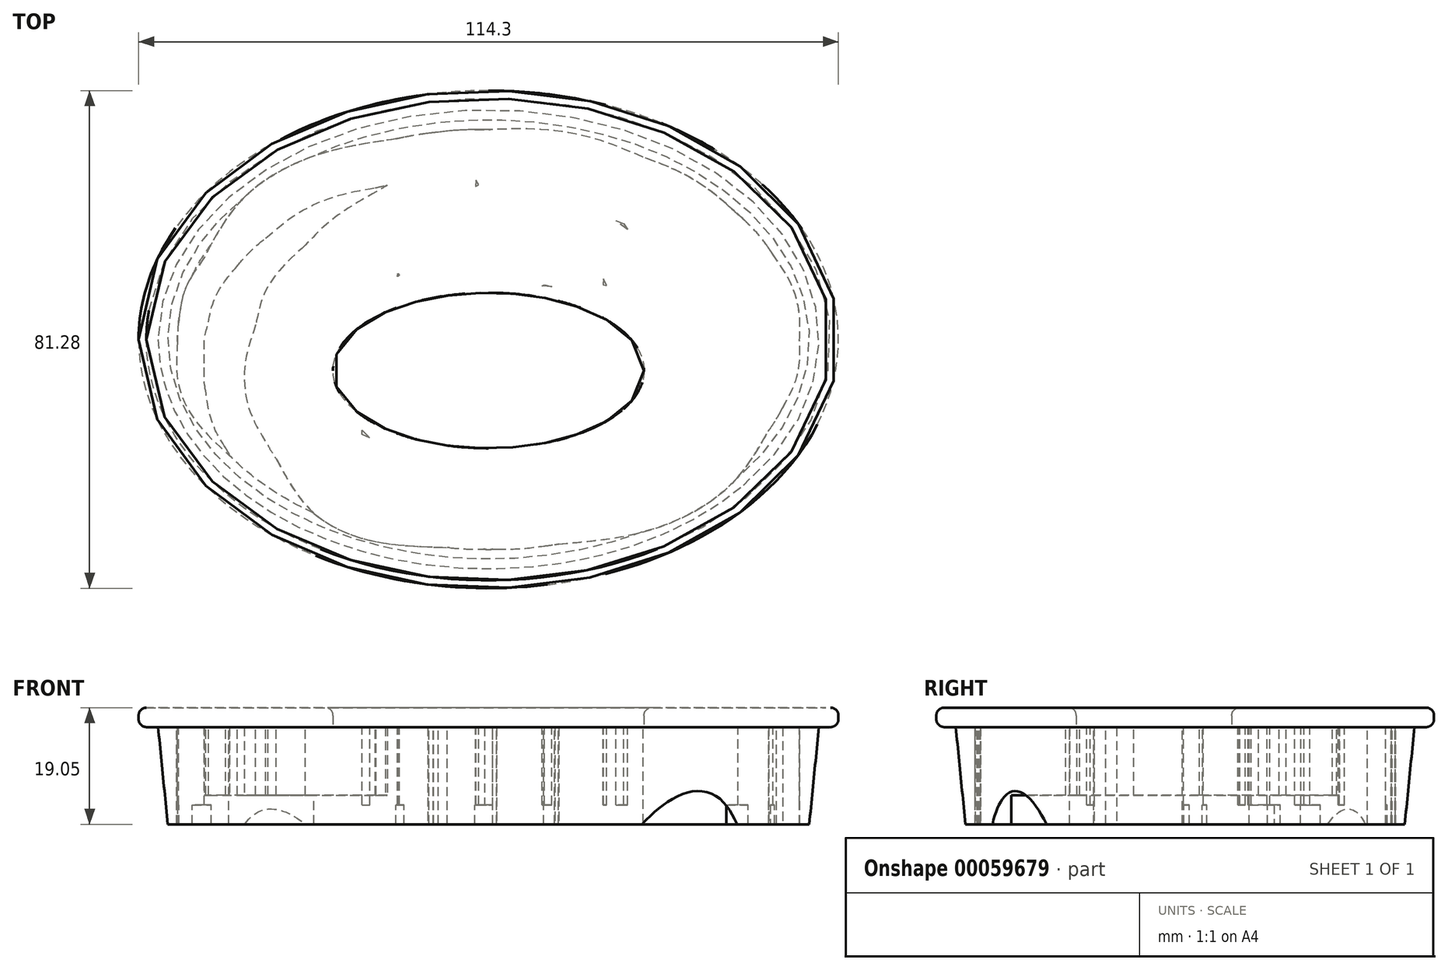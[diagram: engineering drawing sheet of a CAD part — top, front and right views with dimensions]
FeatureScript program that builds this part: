
annotation { "Feature Type Name" : "Feature", "Feature Type Description" : "" }
export const myFeature = defineFeature(function(context is Context, id is Id, definition is map)
    precondition{}
    {
        {
            var Q0;
            Q0=qCreatedBy(makeId("Top.planeOp"),FACE);
            var sketch = newSketch(context, id + "F0", { "sketchPlane" : qUnion([Q0])});
            skEllipse(sketch, "E0", {"center": v(0, 0) * mm, "majorRadius": 37.47 * mm, "minorRadius": 53.97 * mm, "majorAxis": v(0, 1)});
            skSolve(sketch);
        }
        {
            var Q0;
            Q0=makeQuery(id+"F0.imprint","IMPRINT",FACE,{"disambiguationData":[TD([[makeQuery(id+"F0.imprint","IMPRINT",EDGE,{"derivedFrom":sQuery(id+"F0.wireOp",EDGE,"E0")}),1.0]])]});
            extrude(context, id + "F1", {"entities" : qUnion([Q0]), "depth" : 12.7 * mm});
        }
        {
            var Q0;
            Q0=makeQuery(id+"F1.opExtrude","CAP_FACE",FACE,{"disambiguationData":[OSD([sQuery(id+"F0.wireOp",EDGE,"E0")])],"isStart":false});
            var sketch = newSketch(context, id + "F2", { "sketchPlane" : qUnion([Q0])});
            skFitSpline(sketch, "E1", {"points": [v(0.65, 34.29) * mm, v(0.15, 34.29) * mm, v(-0.36, 34.29) * mm, v(-0.87, 34.28) * mm]});
            skFitSpline(sketch, "E2", {"points": [v(-0.87, 34.28) * mm, v(-3.56, 34.22) * mm, v(-5.92, 34.09) * mm, v(-8.17, 33.85) * mm]});
            skFitSpline(sketch, "E3", {"points": [v(-8.17, 33.85) * mm, v(-8.45, 33.82) * mm, v(-8.72, 33.79) * mm, v(-9, 33.76) * mm]});
            skFitSpline(sketch, "E4", {"points": [v(-9, 33.76) * mm, v(-9, 33.76) * mm, v(-9, 33.75) * mm, v(-9.01, 33.75) * mm]});
            skFitSpline(sketch, "E5", {"points": [v(-9.01, 33.75) * mm, v(-9.26, 33.72) * mm, v(-9.5, 33.7) * mm, v(-9.74, 33.66) * mm]});
            skFitSpline(sketch, "E6", {"points": [v(-9.74, 33.66) * mm, v(-9.8, 33.65) * mm, v(-9.85, 33.65) * mm, v(-9.9, 33.64) * mm]});
            skFitSpline(sketch, "E7", {"points": [v(-9.9, 33.64) * mm, v(-11.54, 33.42) * mm, v(-13.16, 33.13) * mm, v(-14.84, 32.77) * mm]});
            skFitSpline(sketch, "E8", {"points": [v(-14.84, 32.77) * mm, v(-29, 29.77) * mm, v(-40.24, 22.86) * mm, v(-46.44, 13.36) * mm]});
            skFitSpline(sketch, "E9", {"points": [v(-46.44, 13.36) * mm, v(-48.86, 9.64) * mm, v(-49.98, 6.83) * mm, v(-50.6, 2.94) * mm]});
            skFitSpline(sketch, "E10", {"points": [v(-50.6, 2.94) * mm, v(-50.72, 2.18) * mm, v(-50.79, 0.96) * mm, v(-50.8, -0.32) * mm]});
            skFitSpline(sketch, "E11", {"points": [v(-50.8, -0.32) * mm, v(-50.8, -0.36) * mm, v(-50.8, -0.4) * mm, v(-50.8, -0.44) * mm]});
            skFitSpline(sketch, "E12", {"points": [v(-50.8, -0.44) * mm, v(-50.67, -7.24) * mm, v(-47.6, -13.57) * mm, v(-42.43, -18.86) * mm]});
            skFitSpline(sketch, "E13", {"points": [v(-42.43, -18.86) * mm, v(-42.38, -18.88) * mm, v(-42.35, -18.89) * mm, v(-42.33, -18.87) * mm]});
            skFitSpline(sketch, "E14", {"points": [v(-42.33, -18.87) * mm, v(-42.31, -18.85) * mm, v(-42.6, -18.32) * mm, v(-42.97, -17.69) * mm]});
            skFitSpline(sketch, "E15", {"points": [v(-42.97, -17.69) * mm, v(-44.53, -15.02) * mm, v(-45.59, -12) * mm, v(-46.2, -8.4) * mm]});
            skFitSpline(sketch, "E16", {"points": [v(-46.2, -8.4) * mm, v(-46.42, -7.15) * mm, v(-46.45, -6.6) * mm, v(-46.45, -3.93) * mm]});
            skFitSpline(sketch, "E17", {"points": [v(-46.45, -3.93) * mm, v(-46.45, -0.59) * mm, v(-46.36, 0.36) * mm, v(-45.76, 2.83) * mm]});
            skFitSpline(sketch, "E18", {"points": [v(-45.76, 2.83) * mm, v(-45.03, 5.85) * mm, v(-43.35, 9.1) * mm, v(-41.04, 11.96) * mm]});
            skFitSpline(sketch, "E19", {"points": [v(-41.04, 11.96) * mm, v(-40.03, 13.2) * mm, v(-37.78, 15.42) * mm, v(-36.4, 16.51) * mm]});
            skFitSpline(sketch, "E20", {"points": [v(-36.4, 16.51) * mm, v(-31.52, 20.37) * mm, v(-25.08, 23.33) * mm, v(-18.5, 24.76) * mm]});
            skFitSpline(sketch, "E21", {"points": [v(-18.5, 24.76) * mm, v(-17.68, 24.93) * mm, v(-16.93, 25.1) * mm, v(-16.82, 25.13) * mm]});
            skFitSpline(sketch, "E22", {"points": [v(-16.82, 25.13) * mm, v(-16.52, 25.2) * mm, v(-16.66, 25.1) * mm, v(-18.39, 24.08) * mm]});
            skFitSpline(sketch, "E23", {"points": [v(-18.39, 24.08) * mm, v(-22.95, 21.4) * mm, v(-26.73, 18.56) * mm, v(-29.95, 15.38) * mm]});
            skFitSpline(sketch, "E24", {"points": [v(-29.95, 15.38) * mm, v(-34.34, 11.03) * mm, v(-36.79, 7.1) * mm, v(-38.03, 2.36) * mm]});
            skFitSpline(sketch, "E25", {"points": [v(-38.03, 2.36) * mm, v(-39.78, -4.3) * mm, v(-39.06, -11.47) * mm, v(-36.05, -17.25) * mm]});
            skFitSpline(sketch, "E26", {"points": [v(-36.05, -17.25) * mm, v(-35.78, -17.77) * mm, v(-35.16, -18.79) * mm, v(-34.67, -19.5) * mm]});
            skFitSpline(sketch, "E27", {"points": [v(-34.67, -19.5) * mm, v(-29, -27.93) * mm, v(-19.76, -32.72) * mm, v(-6.75, -33.99) * mm]});
            skFitSpline(sketch, "E28", {"points": [v(-6.75, -33.99) * mm, v(-6.62, -34) * mm, v(-6.48, -34.01) * mm, v(-6.35, -34.02) * mm]});
            skFitSpline(sketch, "E29", {"points": [v(-6.35, -34.02) * mm, v(-4.75, -34.16) * mm, v(-3.12, -34.25) * mm, v(-1.48, -34.28) * mm]});
            skFitSpline(sketch, "E30", {"points": [v(-1.48, -34.28) * mm, v(-1.2, -34.28) * mm, v(-0.94, -34.28) * mm, v(-0.66, -34.29) * mm]});
            skFitSpline(sketch, "E31", {"points": [v(-0.65, -34.29) * mm, v(-0.22, -34.29) * mm, v(0.21, -34.29) * mm, v(0.65, -34.29) * mm]});
            skFitSpline(sketch, "E32", {"points": [v(0.65, -34.29) * mm, v(0.87, -34.29) * mm, v(1.1, -34.28) * mm, v(1.31, -34.28) * mm]});
            skFitSpline(sketch, "E33", {"points": [v(1.31, -34.28) * mm, v(1.32, -34.28) * mm, v(1.32, -34.28) * mm, v(1.32, -34.28) * mm]});
            skFitSpline(sketch, "E34", {"points": [v(1.32, -34.28) * mm, v(3.93, -34.23) * mm, v(6.5, -34.06) * mm, v(9, -33.75) * mm]});
            skFitSpline(sketch, "E35", {"points": [v(9, -33.75) * mm, v(9.59, -33.68) * mm, v(10.18, -33.6) * mm, v(10.76, -33.52) * mm]});
            skFitSpline(sketch, "E36", {"points": [v(10.76, -33.52) * mm, v(10.8, -33.51) * mm, v(10.83, -33.51) * mm, v(10.86, -33.5) * mm]});
            skFitSpline(sketch, "E37", {"points": [v(10.86, -33.5) * mm, v(11.05, -33.48) * mm, v(11.23, -33.45) * mm, v(11.42, -33.42) * mm]});
            skFitSpline(sketch, "E38", {"points": [v(11.42, -33.42) * mm, v(11.44, -33.42) * mm, v(11.45, -33.41) * mm, v(11.47, -33.41) * mm]});
            skFitSpline(sketch, "E39", {"points": [v(11.47, -33.41) * mm, v(26.6, -31.05) * mm, v(39.16, -24.13) * mm, v(45.76, -14.9) * mm]});
            skFitSpline(sketch, "E40", {"points": [v(45.76, -14.9) * mm, v(45.77, -14.9) * mm, v(45.78, -14.88) * mm, v(45.8, -14.87) * mm]});
            skFitSpline(sketch, "E41", {"points": [v(45.8, -14.87) * mm, v(45.85, -14.79) * mm, v(45.9, -14.71) * mm, v(45.96, -14.63) * mm]});
            skFitSpline(sketch, "E42", {"points": [v(45.96, -14.63) * mm, v(46.33, -14.08) * mm, v(46.7, -13.52) * mm, v(47.04, -12.96) * mm]});
            skFitSpline(sketch, "E43", {"points": [v(47.04, -12.96) * mm, v(47.1, -12.85) * mm, v(47.17, -12.75) * mm, v(47.23, -12.64) * mm]});
            skFitSpline(sketch, "E44", {"points": [v(47.23, -12.64) * mm, v(47.42, -12.32) * mm, v(47.62, -11.96) * mm, v(47.82, -11.6) * mm]});
            skFitSpline(sketch, "E45", {"points": [v(47.82, -11.6) * mm, v(47.89, -11.47) * mm, v(47.96, -11.33) * mm, v(48.03, -11.2) * mm]});
            skFitSpline(sketch, "E46", {"points": [v(48.03, -11.2) * mm, v(49.79, -7.76) * mm, v(50.76, -4.07) * mm, v(50.8, -0.24) * mm]});
            skFitSpline(sketch, "E47", {"points": [v(50.8, -0.24) * mm, v(50.73, 4.5) * mm, v(49.26, 9.4) * mm, v(46.46, 13.83) * mm]});
            skFitSpline(sketch, "E48", {"points": [v(46.46, 13.83) * mm, v(46.19, 14.27) * mm, v(45.92, 14.67) * mm, v(45.65, 15.06) * mm]});
            skFitSpline(sketch, "E49", {"points": [v(45.65, 15.06) * mm, v(44.75, 16.3) * mm, v(43.74, 17.5) * mm, v(42.63, 18.66) * mm]});
            skFitSpline(sketch, "E50", {"points": [v(42.63, 18.66) * mm, v(42.06, 19.21) * mm, v(41.45, 19.77) * mm, v(40.75, 20.37) * mm]});
            skFitSpline(sketch, "E51", {"points": [v(40.75, 20.37) * mm, v(36.13, 24.33) * mm, v(30.95, 27.46) * mm, v(25.29, 29.75) * mm]});
            skFitSpline(sketch, "E52", {"points": [v(25.29, 29.75) * mm, v(25.27, 29.75) * mm, v(25.26, 29.76) * mm, v(25.25, 29.76) * mm]});
            skFitSpline(sketch, "E53", {"points": [v(25.25, 29.76) * mm, v(17.99, 32.58) * mm, v(9.6, 34.21) * mm, v(0.66, 34.29) * mm]});
            skLineSegment(sketch, "E54", {"start": v(-0.66, -34.29) * mm, "end": v(-0.65, -34.29) * mm});
            skLineSegment(sketch, "E55", {"start": v(-0.65, -34.29) * mm, "end": v(-0.66, -34.29) * mm});
            skFitSpline(sketch, "E56", {"points": [v(-6.57, 32.05) * mm, v(-6.5, 32.05) * mm, v(-6.42, 32.05) * mm, v(-6.33, 32.05) * mm]});
            skFitSpline(sketch, "E57", {"points": [v(-6.33, 32.05) * mm, v(-5.68, 32.04) * mm, v(-5.46, 31.99) * mm, v(-4.74, 31.64) * mm]});
            skFitSpline(sketch, "E58", {"points": [v(-4.74, 31.64) * mm, v(-3.54, 31.07) * mm, v(-2.39, 29.9) * mm, v(-1.1, 27.96) * mm]});
            skFitSpline(sketch, "E59", {"points": [v(-1.1, 27.96) * mm, v(0.68, 25.25) * mm, v(0.5, 25.46) * mm, v(1.27, 25.3) * mm]});
            skFitSpline(sketch, "E60", {"points": [v(1.27, 25.3) * mm, v(2.9, 24.97) * mm, v(6.71, 24.05) * mm, v(9.2, 23.38) * mm]});
            skFitSpline(sketch, "E61", {"points": [v(9.2, 23.38) * mm, v(13.33, 22.27) * mm, v(17.31, 20.9) * mm, v(20.79, 19.43) * mm]});
            skLineSegment(sketch, "E62", {"start": v(0.66, 34.29) * mm, "end": v(0.65, 34.29) * mm});
            skLineSegment(sketch, "E63", {"start": v(0.65, 34.29) * mm, "end": v(0.66, 34.29) * mm});
            skFitSpline(sketch, "E64", {"points": [v(22.71, 17.92) * mm, v(24.1, 15.89) * mm, v(25.93, 14.1) * mm, v(28.42, 12.36) * mm]});
            skFitSpline(sketch, "E65", {"points": [v(28.42, 12.36) * mm, v(29.06, 11.92) * mm, v(30.92, 10.75) * mm, v(32.57, 9.77) * mm]});
            skFitSpline(sketch, "E66", {"points": [v(32.57, 9.77) * mm, v(37.35, 6.91) * mm, v(38.63, 6.02) * mm, v(40.52, 4.24) * mm]});
            skFitSpline(sketch, "E67", {"points": [v(40.52, 4.24) * mm, v(42.88, 2.02) * mm, v(43.37, 1.13) * mm, v(43.26, -0.8) * mm]});
            skFitSpline(sketch, "E68", {"points": [v(43.26, -0.8) * mm, v(43.2, -2.07) * mm, v(42.83, -3.14) * mm, v(41.83, -5.05) * mm]});
            skFitSpline(sketch, "E69", {"points": [v(41.83, -5.05) * mm, v(41.14, -6.36) * mm, v(41.11, -6.4) * mm, v(40.27, -7) * mm]});
            skFitSpline(sketch, "E70", {"points": [v(40.27, -7) * mm, v(36.72, -9.6) * mm, v(33.07, -11.56) * mm, v(24.97, -15.2) * mm]});
            skFitSpline(sketch, "E71", {"points": [v(24.97, -15.2) * mm, v(20.2, -17.33) * mm, v(19.15, -17.83) * mm, v(19.15, -17.93) * mm]});
            skFitSpline(sketch, "E72", {"points": [v(19.15, -17.93) * mm, v(19.15, -17.98) * mm, v(19.23, -18.09) * mm, v(19.33, -18.18) * mm]});
            skFitSpline(sketch, "E73", {"points": [v(19.33, -18.18) * mm, v(19.51, -18.34) * mm, v(19.75, -18.27) * mm, v(22.8, -17.26) * mm]});
            skFitSpline(sketch, "E74", {"points": [v(22.8, -17.26) * mm, v(25.87, -16.25) * mm, v(28.54, -15.3) * mm, v(33.23, -13.55) * mm]});
            skFitSpline(sketch, "E75", {"points": [v(33.23, -13.55) * mm, v(34.3, -13.14) * mm, v(35.2, -12.85) * mm, v(35.21, -12.9) * mm]});
            skFitSpline(sketch, "E76", {"points": [v(35.21, -12.9) * mm, v(35.23, -12.94) * mm, v(34.9, -13.87) * mm, v(34.5, -14.96) * mm]});
            skFitSpline(sketch, "E77", {"points": [v(34.5, -14.96) * mm, v(33.03, -18.82) * mm, v(31.79, -20.89) * mm, v(30.17, -22.16) * mm]});
            skFitSpline(sketch, "E78", {"points": [v(30.17, -22.16) * mm, v(29.07, -23.03) * mm, v(28.91, -23.08) * mm, v(27.43, -23.08) * mm]});
            skFitSpline(sketch, "E79", {"points": [v(27.43, -23.08) * mm, v(25.65, -23.08) * mm, v(24.58, -22.94) * mm, v(18.62, -21.98) * mm]});
            skFitSpline(sketch, "E80", {"points": [v(18.62, -21.98) * mm, v(14.63, -21.34) * mm, v(12.63, -21.05) * mm, v(10.97, -20.87) * mm]});
            skFitSpline(sketch, "E81", {"points": [v(10.97, -20.87) * mm, v(10, -20.77) * mm, v(9.76, -20.78) * mm, v(9.32, -20.92) * mm]});
            skFitSpline(sketch, "E82", {"points": [v(9.32, -20.92) * mm, v(8.42, -21.2) * mm, v(4.42, -22.32) * mm, v(2.52, -22.8) * mm]});
            skFitSpline(sketch, "E83", {"points": [v(2.52, -22.8) * mm, v(0.12, -23.42) * mm, v(-3.11, -24.06) * mm, v(-5.31, -24.35) * mm]});
            skFitSpline(sketch, "E84", {"points": [v(-5.31, -24.35) * mm, v(-6.64, -24.52) * mm, v(-7.78, -24.58) * mm, v(-10.03, -24.61) * mm]});
            skFitSpline(sketch, "E85", {"points": [v(-10.03, -24.61) * mm, v(-13.41, -24.66) * mm, v(-13.63, -24.62) * mm, v(-15.25, -23.87) * mm]});
            skFitSpline(sketch, "E86", {"points": [v(-15.25, -23.87) * mm, v(-17.25, -22.92) * mm, v(-18.73, -21.56) * mm, v(-19.56, -19.9) * mm]});
            skFitSpline(sketch, "E87", {"points": [v(-19.56, -19.9) * mm, v(-20.11, -18.78) * mm, v(-20.67, -16.57) * mm, v(-20.67, -15.5) * mm]});
            skLineSegment(sketch, "E88", {"start": v(20.79, 19.43) * mm, "end": v(22.06, 18.88) * mm});
            skLineSegment(sketch, "E89", {"start": v(22.06, 18.88) * mm, "end": v(22.71, 17.92) * mm});
            skLineSegment(sketch, "E90", {"start": v(22.71, 17.92) * mm, "end": v(20.79, 19.43) * mm});
            skFitSpline(sketch, "E91", {"points": [v(-19.37, -16.1) * mm, v(-16.46, -18.96) * mm, v(-13.14, -20.46) * mm, v(-7.96, -21.26) * mm]});
            skFitSpline(sketch, "E92", {"points": [v(-7.96, -21.26) * mm, v(-6.03, -21.56) * mm, v(-0.24, -21.53) * mm, v(2.47, -21.2) * mm]});
            skFitSpline(sketch, "E93", {"points": [v(2.47, -21.2) * mm, v(6.02, -20.78) * mm, v(8.15, -20.39) * mm, v(9.72, -19.86) * mm]});
            skFitSpline(sketch, "E94", {"points": [v(9.72, -19.86) * mm, v(13.27, -18.68) * mm, v(17.67, -16.97) * mm, v(21.08, -15.47) * mm]});
            skFitSpline(sketch, "E95", {"points": [v(21.08, -15.47) * mm, v(23.66, -14.32) * mm, v(27.69, -12.29) * mm, v(28.52, -11.7) * mm]});
            skFitSpline(sketch, "E96", {"points": [v(28.52, -11.7) * mm, v(30.96, -9.98) * mm, v(32.21, -6.97) * mm, v(31.58, -4.39) * mm]});
            skFitSpline(sketch, "E97", {"points": [v(31.58, -4.39) * mm, v(30.67, -0.65) * mm, v(27.91, 2.4) * mm, v(23.17, 4.9) * mm]});
            skFitSpline(sketch, "E98", {"points": [v(23.17, 4.9) * mm, v(21.2, 5.95) * mm, v(17.1, 7.55) * mm, v(15.47, 7.9) * mm]});
            skFitSpline(sketch, "E99", {"points": [v(15.47, 7.9) * mm, v(14.33, 8.16) * mm, v(12.08, 8.47) * mm, v(10.31, 8.61) * mm]});
            skLineSegment(sketch, "E100", {"start": v(-20.67, -15.5) * mm, "end": v(-20.67, -14.83) * mm});
            skLineSegment(sketch, "E101", {"start": v(-20.67, -14.83) * mm, "end": v(-19.37, -16.1) * mm});
            skLineSegment(sketch, "E102", {"start": v(-19.37, -16.1) * mm, "end": v(-20.67, -15.5) * mm});
            skFitSpline(sketch, "E103", {"points": [v(9.15, 8.95) * mm, v(9.37, 9.07) * mm, v(11.34, 9.98) * mm, v(13.52, 10.98) * mm]});
            skFitSpline(sketch, "E104", {"points": [v(13.52, 10.98) * mm, v(17.74, 12.93) * mm, v(17.81, 12.95) * mm, v(18.27, 12.45) * mm]});
            skFitSpline(sketch, "E105", {"points": [v(18.27, 12.45) * mm, v(18.84, 11.84) * mm, v(18.93, 11.4) * mm, v(18.78, 9.85) * mm]});
            skLineSegment(sketch, "E106", {"start": v(10.31, 8.61) * mm, "end": v(8.74, 8.75) * mm});
            skLineSegment(sketch, "E107", {"start": v(8.74, 8.75) * mm, "end": v(9.15, 8.95) * mm});
            skLineSegment(sketch, "E108", {"start": v(9.15, 8.95) * mm, "end": v(10.31, 8.61) * mm});
            skFitSpline(sketch, "E109", {"points": [v(19.31, 8.82) * mm, v(23.55, 7.97) * mm, v(27.51, 6.45) * mm, v(30.52, 4.5) * mm]});
            skFitSpline(sketch, "E110", {"points": [v(30.52, 4.5) * mm, v(32.14, 3.47) * mm, v(32.79, 2.95) * mm, v(34.17, 1.63) * mm]});
            skFitSpline(sketch, "E111", {"points": [v(34.17, 1.63) * mm, v(36.15, -0.27) * mm, v(36.98, -1.56) * mm, v(37.42, -3.42) * mm]});
            skFitSpline(sketch, "E112", {"points": [v(37.42, -3.42) * mm, v(37.61, -4.22) * mm, v(37.64, -5.74) * mm, v(37.48, -6.27) * mm]});
            skFitSpline(sketch, "E113", {"points": [v(37.48, -6.27) * mm, v(37.37, -6.6) * mm, v(37.38, -6.6) * mm, v(37.7, -6.6) * mm]});
            skFitSpline(sketch, "E114", {"points": [v(37.7, -6.6) * mm, v(38.1, -6.6) * mm, v(38.85, -6.3) * mm, v(39.33, -5.93) * mm]});
            skFitSpline(sketch, "E115", {"points": [v(39.33, -5.93) * mm, v(39.51, -5.79) * mm, v(39.92, -5.23) * mm, v(40.23, -4.7) * mm]});
            skFitSpline(sketch, "E116", {"points": [v(40.23, -4.7) * mm, v(41.31, -2.86) * mm, v(41.61, -2.05) * mm, v(41.62, -0.94) * mm]});
            skFitSpline(sketch, "E117", {"points": [v(41.62, -0.94) * mm, v(41.62, 0.34) * mm, v(41.35, 0.78) * mm, v(39.43, 2.68) * mm]});
            skFitSpline(sketch, "E118", {"points": [v(39.43, 2.68) * mm, v(37.14, 4.93) * mm, v(35.34, 6.25) * mm, v(30.26, 9.4) * mm]});
            skFitSpline(sketch, "E119", {"points": [v(30.26, 9.4) * mm, v(24.91, 12.7) * mm, v(24.94, 12.68) * mm, v(23.55, 14.4) * mm]});
            skFitSpline(sketch, "E120", {"points": [v(23.55, 14.4) * mm, v(21.61, 16.81) * mm, v(20.77, 17.5) * mm, v(19.34, 17.8) * mm]});
            skFitSpline(sketch, "E121", {"points": [v(19.34, 17.8) * mm, v(18.32, 18.02) * mm, v(11.2, 18.06) * mm, v(8.82, 17.86) * mm]});
            skFitSpline(sketch, "E122", {"points": [v(8.82, 17.86) * mm, v(2.4, 17.3) * mm, v(-2.34, 16.26) * mm, v(-7.22, 14.3) * mm]});
            skFitSpline(sketch, "E123", {"points": [v(-7.22, 14.3) * mm, v(-9.56, 13.36) * mm, v(-12.38, 11.88) * mm, v(-14.56, 10.44) * mm]});
            skLineSegment(sketch, "E124", {"start": v(18.78, 9.85) * mm, "end": v(18.7, 8.94) * mm});
            skLineSegment(sketch, "E125", {"start": v(18.7, 8.94) * mm, "end": v(19.31, 8.82) * mm});
            skLineSegment(sketch, "E126", {"start": v(19.31, 8.82) * mm, "end": v(18.78, 9.85) * mm});
            skFitSpline(sketch, "E127", {"points": [v(-14.8, 10.77) * mm, v(-13.68, 18.54) * mm, v(-12.16, 24.26) * mm, v(-10.08, 28.49) * mm]});
            skFitSpline(sketch, "E128", {"points": [v(-10.08, 28.49) * mm, v(-9.26, 30.15) * mm, v(-8.6, 31.02) * mm, v(-7.7, 31.64) * mm]});
            skFitSpline(sketch, "E129", {"points": [v(-7.7, 31.64) * mm, v(-7.2, 31.98) * mm, v(-7.07, 32.04) * mm, v(-6.57, 32.05) * mm]});
            skLineSegment(sketch, "E130", {"start": v(-14.56, 10.44) * mm, "end": v(-14.86, 10.25) * mm});
            skLineSegment(sketch, "E131", {"start": v(-14.86, 10.25) * mm, "end": v(-14.8, 10.77) * mm});
            skLineSegment(sketch, "E132", {"start": v(-14.8, 10.77) * mm, "end": v(-14.56, 10.44) * mm});
            skFitSpline(sketch, "E133", {"points": [v(-6.13, 29.92) * mm, v(-6.37, 29.91) * mm, v(-6.6, 29.85) * mm, v(-6.74, 29.75) * mm]});
            skFitSpline(sketch, "E134", {"points": [v(-6.74, 29.75) * mm, v(-7.67, 29.15) * mm, v(-9.63, 24.96) * mm, v(-10.54, 21.61) * mm]});
            skFitSpline(sketch, "E135", {"points": [v(-10.54, 21.61) * mm, v(-10.96, 20.06) * mm, v(-11.8, 15.7) * mm, v(-11.77, 15.16) * mm]});
            skFitSpline(sketch, "E136", {"points": [v(-11.77, 15.16) * mm, v(-11.76, 15.1) * mm, v(-11.7, 15.14) * mm, v(-11.64, 15.25) * mm]});
            skFitSpline(sketch, "E137", {"points": [v(-11.64, 15.25) * mm, v(-9.62, 18.3) * mm, v(-8.7, 19.5) * mm, v(-7.06, 21.18) * mm]});
            skFitSpline(sketch, "E138", {"points": [v(-7.06, 21.18) * mm, v(-5.38, 22.9) * mm, v(-3.63, 24.25) * mm, v(-2.12, 24.98) * mm]});
            skFitSpline(sketch, "E139", {"points": [v(-2.04, 26.01) * mm, v(-2.77, 27.4) * mm, v(-4.42, 29.34) * mm, v(-5.22, 29.75) * mm]});
            skFitSpline(sketch, "E140", {"points": [v(-5.22, 29.75) * mm, v(-5.47, 29.88) * mm, v(-5.81, 29.94) * mm, v(-6.13, 29.92) * mm]});
            skLineSegment(sketch, "E141", {"start": v(-2.12, 24.98) * mm, "end": v(-1.62, 25.22) * mm});
            skLineSegment(sketch, "E142", {"start": v(-1.62, 25.22) * mm, "end": v(-2.04, 26.01) * mm});
            skLineSegment(sketch, "E143", {"start": v(-2.04, 26.01) * mm, "end": v(-2.12, 24.98) * mm});
            skSolve(sketch);
        }
        {
            var Q0;
            Q0=makeQuery(id+"F2.imprint","IMPRINT",FACE,{"disambiguationData":[TD([[makeQuery(id+"F2.imprint","IMPRINT",EDGE,{"derivedFrom":sQuery(id+"F2.wireOp",EDGE,"E1")}),1.0]])]});
            var Q1;
            Q1=makeQuery(id+"F2.imprint","IMPRINT",FACE,{"disambiguationData":[TD([[makeQuery(id+"F2.imprint","IMPRINT",EDGE,{"derivedFrom":sQuery(id+"F2.wireOp",EDGE,"E133")}),1.0]])]});
            extrude(context, id + "F3", {"entities" : qUnion([Q0, Q1]), "operationType" : NewBodyOperationType.REMOVE, "oppositeDirection" : true, "depth" : 25.4 * mm});
        }
        {
            var Q0;
            {var subQ0=sQuery(id+"F0.wireOp",EDGE,"E0");Q0=makeQuery(id+"F3.boolean.opBoolean","SPLIT",FACE,{"disambiguationData":[TD([makeQuery(id+"F1.opExtrude","SWEPT_FACE",FACE,{"disambiguationData":[OSD([subQ0])]})])],"derivedFrom":makeQuery(id+"F1.opExtrude","CAP_FACE",FACE,{"disambiguationData":[OSD([subQ0])],"isStart":false})});}
            var sketch = newSketch(context, id + "F4", { "sketchPlane" : qUnion([Q0])});
            skEllipse(sketch, "E144", {"center": v(0, 0) * mm, "majorRadius": 40.64 * mm, "minorRadius": 57.15 * mm, "majorAxis": v(0, 1)});
            skSolve(sketch);
        }
        {
            var Q0;
            Q0 = qSketchRegion(id + "F4", true);
            extrude(context, id + "F5", {"entities" : qUnion([Q0]), "operationType" : NewBodyOperationType.ADD, "depth" : 3.17 * mm});
        }
        {
            var Q0;
            {var subQ0=sQuery(id+"F0.wireOp",EDGE,"E0");Q0=makeQuery(id+"F3.boolean.opBoolean","SPLIT",FACE,{"disambiguationData":[TD([makeQuery(id+"F1.opExtrude","SWEPT_FACE",FACE,{"disambiguationData":[OSD([subQ0])]})])],"derivedFrom":makeQuery(id+"F1.opExtrude","CAP_FACE",FACE,{"disambiguationData":[OSD([subQ0])],"isStart":true})});}
            var sketch = newSketch(context, id + "F6", { "sketchPlane" : qUnion([Q0])});
            skEllipse(sketch, "E145", {"center": v(0, 0) * mm, "majorRadius": 53.98 * mm, "minorRadius": 37.47 * mm, "majorAxis": v(1, 0)});
            skEllipse(sketch, "E146", {"center": v(0, 0) * mm, "majorRadius": 34.3 * mm, "minorRadius": 50.8 * mm, "majorAxis": v(0, 1)});
            skSolve(sketch);
        }
        {
            var Q0;
            Q0=makeQuery(id+"F6.imprint","IMPRINT",FACE,{"disambiguationData":[TD([[makeQuery(id+"F6.imprint","IMPRINT",EDGE,{"derivedFrom":sQuery(id+"F6.wireOp",EDGE,"E145")}),-1.0]])]});
            extrude(context, id + "F7", {"entities" : qUnion([Q0]), "operationType" : NewBodyOperationType.ADD, "depth" : 3.17 * mm});
        }
        {
            var Q0;
            Q0=makeQuery(id+"F7.opExtrude","CAP_EDGE",EDGE,{"disambiguationData":[OSD([sQuery(id+"F6.wireOp",EDGE,"E145")])],"isStart":false});
            chamfer(context, id + "F8", {"entities" : qUnion([Q0]), "chamferType" : ChamferType.TWO_OFFSETS, "width1" : 15.88 * mm, "oppositeDirection" : false, "width2" : 1.59 * mm, "tangentPropagation" : true});
        }
        {
            var Q0;
            {var subQ3=sQuery(id+"F2.wireOp",EDGE,"E13");var subQ4=makeQuery(id+"F3.opExtrude","SWEPT_FACE",FACE,{"disambiguationData":[OSD([subQ3])]});var subQ15=sQuery(id+"F0.wireOp",EDGE,"E0");var subQ16=makeQuery(id+"F1.opExtrude","CAP_FACE",FACE,{"disambiguationData":[OSD([subQ15])],"isStart":true});Q0=makeQuery(id+"F7.boolean.opBoolean","SPLIT",FACE,{"disambiguationData":[TD([makeQuery(id+"F3.boolean.opBoolean","COPY",FACE,{"derivedFrom":subQ4})])],"derivedFrom":makeQuery(id+"F3.boolean.opBoolean","SPLIT",FACE,{"disambiguationData":[TD([makeQuery(id+"F1.opExtrude","SWEPT_FACE",FACE,{"disambiguationData":[OSD([subQ15])]})])],"derivedFrom":subQ16})});}
            var Q1;
            Q1=makeQuery(id+"F3.boolean.opBoolean","SPLIT",FACE,{"disambiguationData":[TD([makeQuery(id+"F3.opExtrude","SWEPT_FACE",FACE,{"disambiguationData":[OSD([sQuery(id+"F2.wireOp",EDGE,"E56")])]})])],"derivedFrom":makeQuery(id+"F1.opExtrude","CAP_FACE",FACE,{"disambiguationData":[OSD([sQuery(id+"F0.wireOp",EDGE,"E0")])],"isStart":true})});
            extrude(context, id + "F9", {"entities" : qUnion([Q0, Q1]), "operationType" : NewBodyOperationType.REMOVE, "oppositeDirection" : true, "depth" : 1.59 * mm});
        }
        {
            var Q0;
            Q0=makeQuery(id+"F5.boolean.opBoolean","SPLIT",FACE,{"disambiguationData":[TD([makeQuery(id+"F3.boolean.opBoolean","COPY",FACE,{"derivedFrom":makeQuery(id+"F3.opExtrude","SWEPT_FACE",FACE,{"disambiguationData":[OSD([sQuery(id+"F2.wireOp",EDGE,"E1")])]})})])],"derivedFrom":makeQuery(id+"F5.opExtrude","CAP_FACE",FACE,{"disambiguationData":[OSD([sQuery(id+"F4.wireOp",EDGE,"E144")])],"isStart":true})});
            var sketch = newSketch(context, id + "F10", { "sketchPlane" : qUnion([Q0])});
            skEllipse(sketch, "E147", {"center": v(0, 5.08) * mm, "majorRadius": 25.4 * mm, "minorRadius": 12.7 * mm, "majorAxis": v(1, 0)});
            skSolve(sketch);
        }
        {
            var Q0;
            Q0=makeQuery(id+"F10.imprint","IMPRINT",FACE,{"disambiguationData":[TD([[makeQuery(id+"F10.imprint","IMPRINT",EDGE,{"derivedFrom":sQuery(id+"F10.wireOp",EDGE,"E147")}),1.0]])]});
            extrude(context, id + "F11", {"entities" : qUnion([Q0]), "operationType" : NewBodyOperationType.REMOVE, "oppositeDirection" : true, "depth" : 25.4 * mm});
        }
        {
            var Q0;
            Q0=makeQuery(id+"F5.opExtrude","CAP_EDGE",EDGE,{"disambiguationData":[OSD([sQuery(id+"F4.wireOp",EDGE,"E144")])],"isStart":true});
            var Q1;
            Q1=makeQuery(id+"F5.opExtrude","CAP_EDGE",EDGE,{"disambiguationData":[OSD([sQuery(id+"F4.wireOp",EDGE,"E144")])],"isStart":false});
            fillet(context, id + "F12", {"entities" : qUnion([Q0, Q1]), "radius" : 1.27 * mm, "tangentPropagation" : true, "allowEdgeOverflow" : false});
        }
        {
            var Q0;
            Q0=makeQuery(id+"F11.boolean.opBoolean","INTERSECT",EDGE,{"derivedFrom":[makeQuery(id+"F5.opExtrude","CAP_FACE",FACE,{"disambiguationData":[OSD([sQuery(id+"F4.wireOp",EDGE,"E144")])],"isStart":false}),makeQuery(id+"F11.opExtrude","SWEPT_FACE",FACE,{"disambiguationData":[OSD([sQuery(id+"F10.wireOp",EDGE,"E147")])]})]});
            var Q1;
            Q1=makeQuery(id+"F11.boolean.opBoolean","COPY",EDGE,{"derivedFrom":makeQuery(id+"F11.opExtrude","CAP_EDGE",EDGE,{"disambiguationData":[OSD([sQuery(id+"F10.wireOp",EDGE,"E147")])],"isStart":true})});
            fillet(context, id + "F13", {"entities" : qUnion([Q0, Q1]), "radius" : 1.27 * mm, "tangentPropagation" : true, "allowEdgeOverflow" : false});
        }
        {
            var Q0;
            Q0=makeQuery(id+"F3.boolean.opBoolean","SPLIT",BODY,{"disambiguationData":[OD(0.0)],"derivedFrom":makeQuery(id+"F1.opExtrude","SWEPT_BODY",BODY,{"disambiguationData":[OSD([sQuery(id+"F0.wireOp",EDGE,"E0")])]})});
            transform(context, id + "F14", {"entities" : qUnion([Q0]), "transformType" : TransformType.TRANSLATION_3D, "dx" : 0 * mm, "dy" : 0 * mm, "dz" : 3.17 * mm, "makeCopy" : false});
        }
    });
